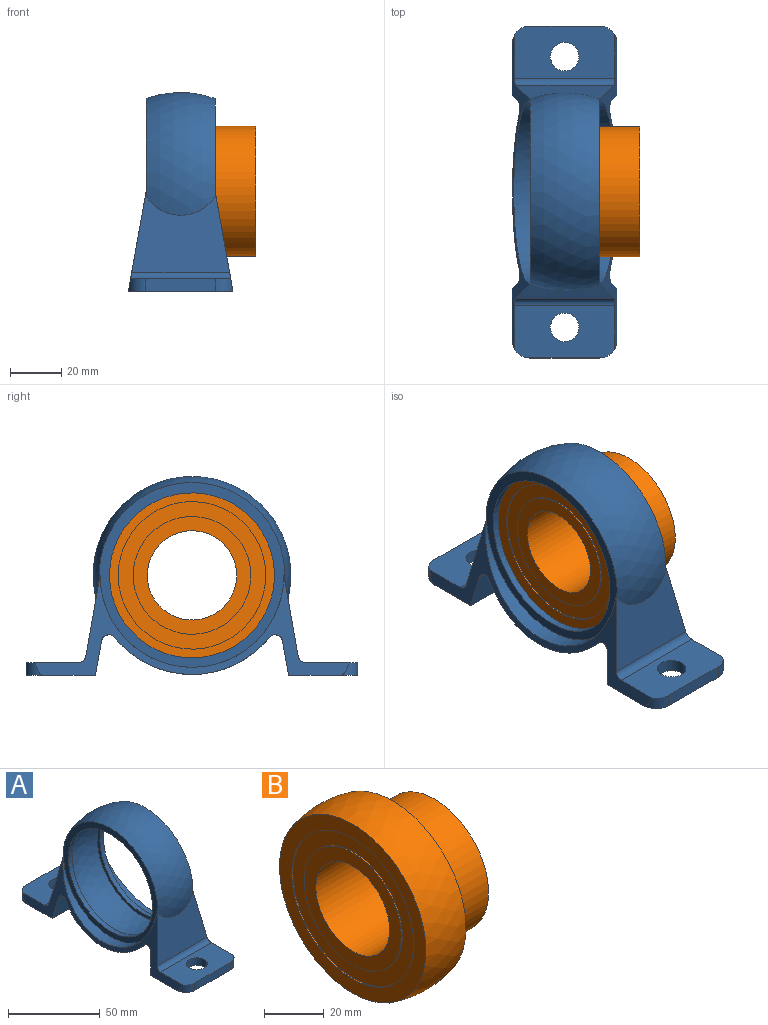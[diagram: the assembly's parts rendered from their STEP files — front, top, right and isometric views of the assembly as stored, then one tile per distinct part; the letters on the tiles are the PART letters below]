
ASSEMBLY  parts=2 mates=1
PART A: 33 faces, bbox 41x130x78 mm
  f0: cylinder r=36mm len=72mm, axis (1,0,0), area 462.9mm2, adj f18,f25
  f1: plane 41x13.45mm, normal (0,0.98,-0.17), area 527mm2, adj f8,f9,f25,f26
  f2: cylinder r=38.8mm len=60.35mm, axis (1,0,0), area 2703.3mm2, adj f7,f8,f25,f26
  f3: cylinder r=36mm len=72mm, axis (1,0,0), area 462.9mm2, adj f12,f26
  f4: plane 41x27.17mm, normal (0,0,-1), area 995.2mm2, adj f5,f6,f25,f26,f29,f30,f32
  f5: plane 27.33x5mm, normal (0,1,0), area 136.7mm2, adj f4,f20,f29,f30
  f6: plane 41x13.45mm, normal (0,-0.98,-0.17), area 527mm2, adj f4,f7,f25,f26
  f7: cylinder r=3mm len=36.2mm, axis (1,0,0), area 244mm2, adj f2,f6,f25,f26
  f8: cylinder r=3mm len=36.2mm, axis (1,0,0), area 244mm2, adj f1,f2,f25,f26
  f9: plane 41x27.17mm, normal (0,0,-1), area 995.2mm2, adj f1,f10,f25,f26,f27,f28,f31
  f10: plane 27.33x5mm, normal (0,-1,0), area 136.7mm2, adj f9,f11,f27,f28
  f11: plane 39.21x20.45mm, normal (0,0,1), area 691.6mm2, adj f10,f24,f25,f26,f27,f28,f31
  f12: plane 72.75x72.38mm, normal (1,0,0), area 836.1mm2, adj f3,f13,f19,f22,f23
  f13: cylinder r=32.31mm len=64.61mm, axis (-1,0,0), area 568.4mm2, adj f12,f14
  f14: plane 68.75x68.75mm, normal (-1,0,0), area 433mm2, adj f13,f15
  f15: sphere r=36mm, area 4840.6mm2, adj f14,f16
  f16: plane 68.75x68.75mm, normal (1,0,0), area 433mm2, adj f15,f17
  f17: cylinder r=32.31mm len=64.61mm, axis (-1,0,0), area 568.4mm2, adj f16,f18
  f18: plane 72.75x72.38mm, normal (-1,0,0), area 836.1mm2, adj f0,f17,f19,f22,f23
  f19: sphere r=38.8mm, area 3687.3mm2, adj f12,f18,f22,f23
  f20: plane 39.21x20.45mm, normal (0,0,1), area 691.6mm2, adj f5,f21,f25,f26,f29,f30,f32
  f21: cylinder r=3mm len=39.21mm, axis (1,0,0), area 162.9mm2, adj f20,f22,f25,f26
  f22: plane 38.33x31.72mm, normal (0,0.98,0.17), area 855.5mm2, adj f12,f18,f19,f21,f25,f26
  f23: plane 38.33x31.72mm, normal (0,-0.98,0.17), area 855.5mm2, adj f12,f18,f19,f24,f25,f26
  f24: cylinder r=3mm len=39.21mm, axis (1,0,0), area 162.9mm2, adj f11,f23,f25,f26
  f25: plane 123.09x39.2mm, normal (-0.98,0,0.18), area 768.4mm2, adj f0,f1,f2,f4,f6,f7,f8,f9
  f26: plane 123.09x39.2mm, normal (0.98,0,0.18), area 768.4mm2, adj f1,f2,f3,f4,f6,f7,f8,f9
  f27: cylinder r=6.83mm len=6.83mm, axis (0,0,1), area 41.9mm2, adj f9,f10,f11,f26
  f28: cylinder r=6.83mm len=6.83mm, axis (0,0,1), area 41.9mm2, adj f9,f10,f11,f25
  f29: cylinder r=6.83mm len=6.83mm, axis (0,0,1), area 41.9mm2, adj f4,f5,f20,f26
  f30: cylinder r=6.83mm len=6.83mm, axis (0,0,1), area 41.9mm2, adj f4,f5,f20,f25
  f31: cylinder r=5.6mm len=11.2mm, axis (0,0,1), area 175.9mm2, adj f9,f11
  f32: cylinder r=5.6mm len=11.2mm, axis (0,0,1), area 175.9mm2, adj f4,f20
PART B: 14 faces, bbox 38.9x72x72 mm
  f0: cylinder r=23.05mm len=46.1mm, axis (-1,0,0), area 73.9mm2, adj f1,f13
  f1: plane 46.1x46.1mm, normal (-1,0,0), area 707mm2, adj f0,f2
  f2: cylinder r=17.5mm len=38.9mm, axis (-1,0,0), area 4277.3mm2, adj f1,f3
  f3: plane 51.1x51.1mm, normal (1,0,0), area 1088.7mm2, adj f2,f4
  f4: cylinder r=25.55mm len=51.1mm, axis (-1,0,0), area 2809.4mm2, adj f3,f5
  f5: plane 51.1x51.1mm, normal (-1,0,0), area 381.7mm2, adj f4,f6
  f6: cylinder r=23.05mm len=46.1mm, axis (-1,0,0), area 418.6mm2, adj f5,f7
  f7: plane 57.77x57.77mm, normal (1,0,0), area 952.4mm2, adj f6,f8
  f8: cylinder r=28.89mm len=57.77mm, axis (-1,0,0), area 90.8mm2, adj f7,f9
  f9: plane 69.45x69.45mm, normal (1,0,0), area 1166.5mm2, adj f8,f10
  f10: sphere r=36mm, area 4297.7mm2, adj f9,f11
  f11: plane 69.45x69.45mm, normal (-1,0,0), area 1166.5mm2, adj f10,f12
  f12: cylinder r=28.89mm len=57.77mm, axis (-1,0,0), area 90.8mm2, adj f11,f13
  f13: plane 57.77x57.77mm, normal (-1,0,0), area 952.4mm2, adj f0,f12
PLACE A at identity fixed
PLACE B at identity
MATE fastened B.f0 <-> A.f0  axis (-1,0,0) through (0,0,0)mm
